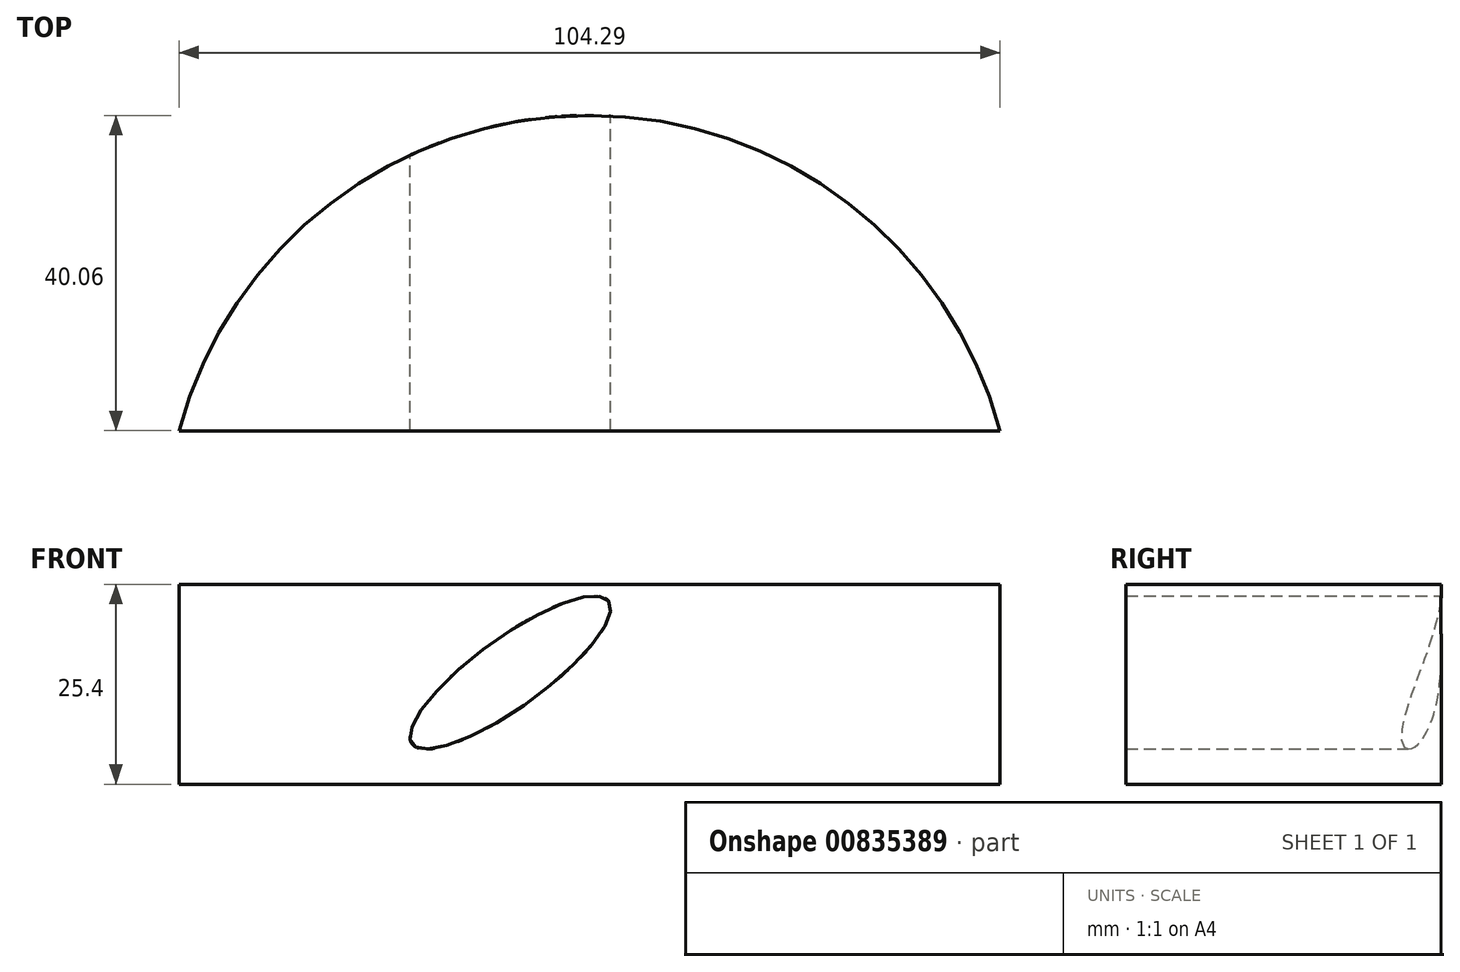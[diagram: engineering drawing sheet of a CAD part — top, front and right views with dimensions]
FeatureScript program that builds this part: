
annotation { "Feature Type Name" : "Feature", "Feature Type Description" : "" }
export const myFeature = defineFeature(function(context is Context, id is Id, definition is map)
    precondition{}
    {
        {
            var Q0;
            Q0=qCreatedBy(makeId("Top.planeOp"),FACE);
            var sketch = newSketch(context, id + "F0", { "sketchPlane" : qUnion([Q0])});
            skLineSegment(sketch, "E0", {"start": v(-55.77, 62) * mm, "end": v(48.52, 62) * mm});
            skArc(sketch, "E1", {"start": v(48.52, 62) * mm, "mid": v(-3.62, 102.06) * mm, "end": v(-55.77, 62) * mm});
            skSolve(sketch);
        }
        {
            var Q0;
            Q0=makeQuery(id+"F0.imprint","IMPRINT",FACE,{"disambiguationData":[TD([[makeQuery(id+"F0.imprint","IMPRINT",EDGE,{"derivedFrom":sQuery(id+"F0.wireOp",EDGE,"E0")}),1.0]])]});
            extrude(context, id + "F1", {"entities" : qUnion([Q0]), "depth" : 25.4 * mm, "offsetDistance" : 25.4 * mm});
        }
        {
            var Q0;
            Q0=makeQuery(id+"F1.opExtrude","SWEPT_FACE",FACE,{"disambiguationData":[OSD([sQuery(id+"F0.wireOp",EDGE,"E0")])]});
            var sketch = newSketch(context, id + "F2", { "sketchPlane" : qUnion([Q0])});
            skEllipse(sketch, "E2", {"center": v(-13.68, 14.19) * mm, "majorRadius": 15.44 * mm, "minorRadius": 4.4 * mm, "majorAxis": v(0.8, 0.59)});
            skSolve(sketch);
        }
        {
            var Q0;
            Q0=makeQuery(id+"F2.imprint","IMPRINT",FACE,{"disambiguationData":[TD([[makeQuery(id+"F2.imprint","IMPRINT",EDGE,{"derivedFrom":sQuery(id+"F2.wireOp",EDGE,"E2")}),1.0]])]});
            var sketch = newSketch(context, id + "F3", { "sketchPlane" : qUnion([Q0])});
            skSolve(sketch);
        }
        {
            var Q0;
            Q0=makeQuery(id+"F3.imprint","IMPRINT",FACE,{"disambiguationData":[TD([[makeQuery(id+"F3.imprint","IMPRINT",EDGE,{"derivedFrom":makeQuery(id+"F2.imprint","IMPRINT",EDGE,{"derivedFrom":sQuery(id+"F2.wireOp",EDGE,"E2")})}),1.0]])]});
            extrude(context, id + "F4", {"entities" : qUnion([Q0]), "operationType" : NewBodyOperationType.REMOVE, "endBound" : BoundingType.THROUGH_ALL, "oppositeDirection" : true, "depth" : 25.4 * mm, "offsetDistance" : 25.4 * mm});
        }
    });
